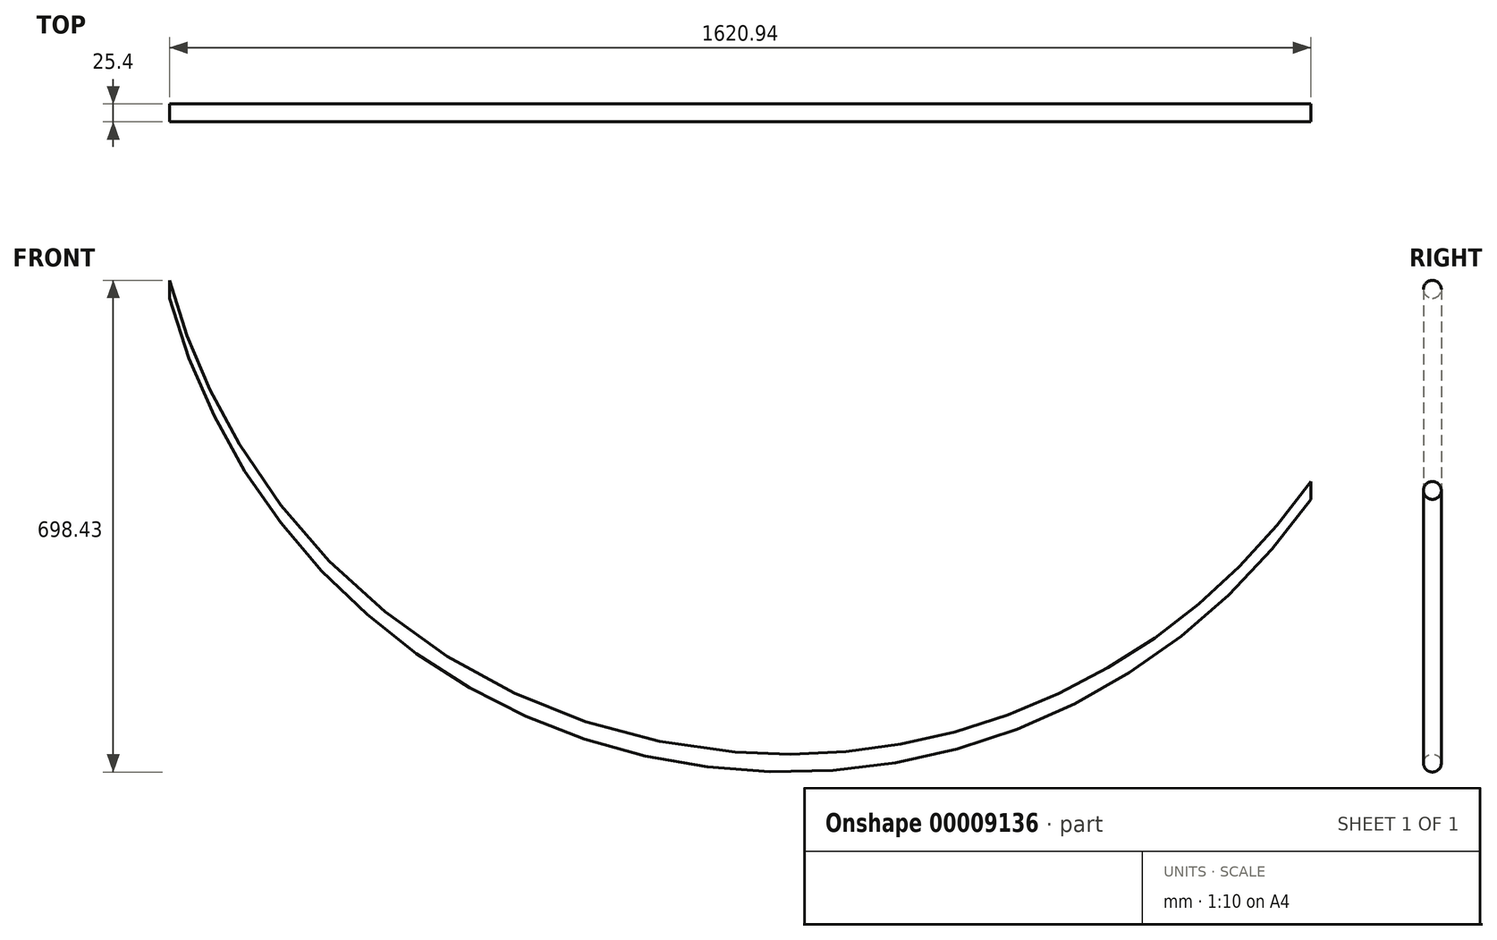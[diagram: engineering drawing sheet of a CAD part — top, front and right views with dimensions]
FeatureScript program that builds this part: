
annotation { "Feature Type Name" : "Feature", "Feature Type Description" : "" }
export const myFeature = defineFeature(function(context is Context, id is Id, definition is map)
    precondition{}
    {
        {
            var Q0;
            Q0=qCreatedBy(makeId("Front.planeOp"),FACE);
            var sketch = newSketch(context, id + "F0", { "sketchPlane" : qUnion([Q0])});
            skArc(sketch, "E0", {"start": v(-877.1, -235.02) * mm, "mid": v(-157.68, -894.25) * mm, "end": v(743.83, -520.84) * mm});
            skLineSegment(sketch, "E1", {"start": v(0, 0) * mm, "end": v(0, -1245.87) * mm, "construction": true});
            skLineSegment(sketch, "E2", {"start": v(0, 0) * mm, "end": v(-1306.85, -350.17) * mm, "construction": true});
            skLineSegment(sketch, "E3", {"start": v(0, 0) * mm, "end": v(982.73, -688.12) * mm, "construction": true});
            skSolve(sketch);
        }
        {
            var Q0;
            Q0=qCreatedBy(makeId("Right.planeOp"),FACE);
            var sketch = newSketch(context, id + "F1", { "sketchPlane" : qUnion([Q0])});
            skCircle(sketch, "E4", {"center": v(0, -908.05) * mm, "radius": 12.7 * mm});
            skSolve(sketch);
        }
        {
            var Q0;
            Q0=makeQuery(id+"F1.imprint","IMPRINT",FACE,{"disambiguationData":[TD([[makeQuery(id+"F1.imprint","IMPRINT",EDGE,{"derivedFrom":sQuery(id+"F1.wireOp",EDGE,"E4")}),1.0]])]});
            var Q1;
            Q1=sQuery(id+"F0.wireOp",EDGE,"E0");
            sweep(context, id + "F2", {"profiles" : qUnion([Q0]), "path" : qUnion([Q1]), "keepProfileOrientation" : true});
        }
    });
